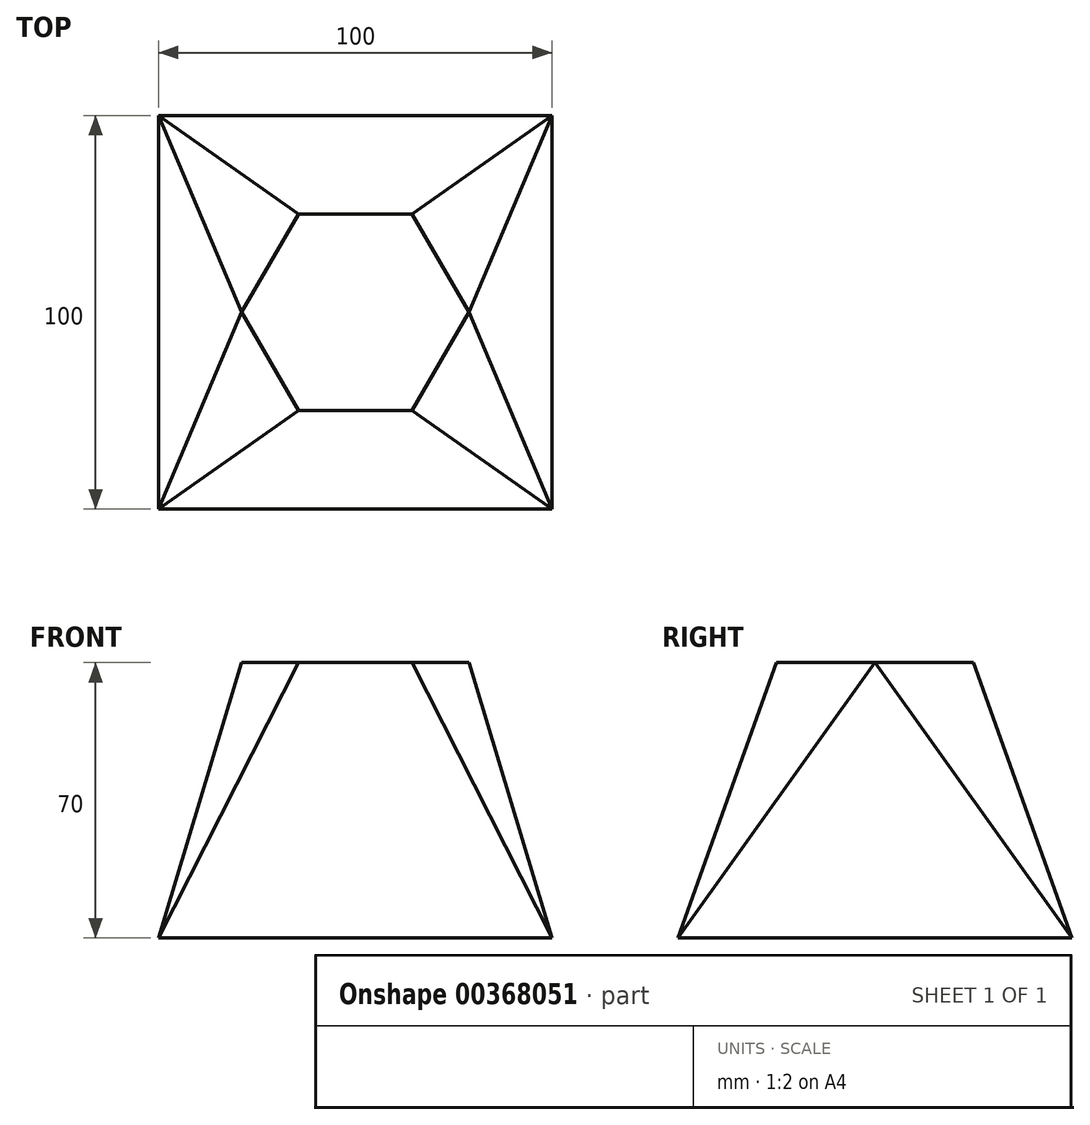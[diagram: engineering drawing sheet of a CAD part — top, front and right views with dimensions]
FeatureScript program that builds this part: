
annotation { "Feature Type Name" : "Feature", "Feature Type Description" : "" }
export const myFeature = defineFeature(function(context is Context, id is Id, definition is map)
    precondition{}
    {
        {
            var Q0;
            Q0=qCreatedBy(makeId("Top.planeOp"),FACE);
            var sketch = newSketch(context, id + "F0", { "sketchPlane" : qUnion([Q0])});
            skLineSegment(sketch, "E0.bottom", {"start": v(-50, 50) * mm, "end": v(50, 50) * mm});
            skLineSegment(sketch, "E0.top", {"start": v(-50, -50) * mm, "end": v(50, -50) * mm});
            skLineSegment(sketch, "E0.left", {"start": v(-50, 50) * mm, "end": v(-50, -50) * mm});
            skLineSegment(sketch, "E0.right", {"start": v(50, 50) * mm, "end": v(50, -50) * mm});
            skSolve(sketch);
        }
        {
            var Q0;
            Q0=qCreatedBy(makeId("Top.planeOp"),FACE);
            cPlane(context, id + "F1", {"entities" : qUnion([Q0]), "cplaneType" : CPlaneType.OFFSET, "offset" : 70 * mm, "width" : 150 * mm, "height" : 150 * mm});
        }
        {
            var Q0;
            Q0=qCreatedBy(id+"F1.planeOp",FACE);
            var sketch = newSketch(context, id + "F2", { "sketchPlane" : qUnion([Q0])});
            skCircle(sketch, "E1.cCircle", {"center": v(0, 0) * mm, "radius": 25 * mm, "construction": true});
            skLineSegment(sketch, "E1.0", {"start": v(-14.43, 25) * mm, "end": v(14.43, 25) * mm});
            skLineSegment(sketch, "E1.1", {"start": v(14.43, 25) * mm, "end": v(28.87, 0) * mm});
            skLineSegment(sketch, "E1.2", {"start": v(28.87, 0) * mm, "end": v(14.43, -25) * mm});
            skLineSegment(sketch, "E1.3", {"start": v(14.43, -25) * mm, "end": v(-14.43, -25) * mm});
            skLineSegment(sketch, "E1.4", {"start": v(-14.43, -25) * mm, "end": v(-28.87, 0) * mm});
            skLineSegment(sketch, "E1.5", {"start": v(-28.87, 0) * mm, "end": v(-14.43, 25) * mm});
            skPoint(sketch, "E1.0.midPoint", {"position": v(0, 25) * mm});
            skLineSegment(sketch, "E2", {"start": v(-14.43, 25) * mm, "end": v(-14.43, -25) * mm});
            skLineSegment(sketch, "E3", {"start": v(14.43, 25) * mm, "end": v(14.43, -25) * mm});
            skSolve(sketch);
        }
        {
            var Q0;
            Q0=makeQuery(id+"F0.imprint","IMPRINT",FACE,{"disambiguationData":[TD([[makeQuery(id+"F0.imprint","IMPRINT",EDGE,{"derivedFrom":sQuery(id+"F0.wireOp",EDGE,"E0.bottom")}),-1.0]])]});
            var Q1;
            Q1=makeQuery(id+"F2.imprint","IMPRINT",FACE,{"disambiguationData":[TD([[makeQuery(id+"F2.imprint","IMPRINT",EDGE,{"derivedFrom":sQuery(id+"F2.wireOp",EDGE,"E1.0")}),-1.0]])]});
            loft(context, id + "F3", {"sheetProfilesArray" : [{ "sheetProfileEntities" : qUnion([Q0]) }, { "sheetProfileEntities" : qUnion([Q1]) }]});
        }
        {
            var Q1;
            Q1=makeQuery(id+"F2.imprint","IMPRINT",FACE,{"disambiguationData":[TD([[makeQuery(id+"F2.imprint","IMPRINT",EDGE,{"derivedFrom":sQuery(id+"F2.wireOp",EDGE,"E1.4")}),-1.0]])]});
            var Q2;
            Q2=makeQuery(id+"F3.opLoft","MID_CAP_VERTEX",VERTEX,{"disambiguationData":[OSD([sQuery(id+"F0.wireOp",EDGE,"E0.bottom"),sQuery(id+"F0.wireOp",EDGE,"E0.left")])],"capPos":0.0});
            loft(context, id + "F4", {"operationType" : NewBodyOperationType.ADD, "sheetProfilesArray" : [{ "sheetProfileEntities" : qUnion([Q1]) }, { "sheetProfileEntities" : qUnion([Q2]) }]});
        }
        {
            var Q1;
            Q1=makeQuery(id+"F2.imprint","IMPRINT",FACE,{"disambiguationData":[TD([[makeQuery(id+"F2.imprint","IMPRINT",EDGE,{"derivedFrom":sQuery(id+"F2.wireOp",EDGE,"E1.4")}),-1.0]])]});
            var Q2;
            Q2=makeQuery(id+"F3.opLoft","MID_CAP_VERTEX",VERTEX,{"disambiguationData":[OSD([sQuery(id+"F0.wireOp",EDGE,"E0.top"),sQuery(id+"F0.wireOp",EDGE,"E0.left")])],"capPos":0.0});
            loft(context, id + "F5", {"operationType" : NewBodyOperationType.ADD, "sheetProfilesArray" : [{ "sheetProfileEntities" : qUnion([Q1]) }, { "sheetProfileEntities" : qUnion([Q2]) }]});
        }
        {
            var Q1;
            Q1=makeQuery(id+"F5.opLoft","SWEPT_FACE",FACE,{"disambiguationData":[OSD([sQuery(id+"F2.wireOp",EDGE,"E1.0"),sQuery(id+"F2.wireOp",EDGE,"E1.4"),sQuery(id+"F2.wireOp",EDGE,"E1.5"),sQuery(id+"F2.wireOp",EDGE,"E2")])]});
            var Q2;
            Q2=makeQuery(id+"F4.opLoft","SWEPT_FACE",FACE,{"disambiguationData":[OSD([sQuery(id+"F2.wireOp",EDGE,"E1.3"),sQuery(id+"F2.wireOp",EDGE,"E1.4"),sQuery(id+"F2.wireOp",EDGE,"E1.5"),sQuery(id+"F2.wireOp",EDGE,"E2")])]});
            var Q3;
            {var subQ0=sQuery(id+"F0.wireOp",EDGE,"E0.left");var subQ1=sQuery(id+"F0.wireOp",EDGE,"E0.top");Q3=makeQuery(id+"F5.boolean.opBoolean","MERGE",VERTEX,{"derivedFrom":[makeQuery(id+"F3.opLoft","MID_CAP_VERTEX",VERTEX,{"disambiguationData":[OSD([subQ1,subQ0])],"capPos":0.0}),makeQuery(id+"F5.opLoft","SWEPT_VERTEX",VERTEX,{"disambiguationData":[OSD([subQ1,subQ0,sQuery(id+"F2.wireOp",EDGE,"E1.3"),sQuery(id+"F2.wireOp",EDGE,"E1.4"),sQuery(id+"F2.wireOp",EDGE,"E2")])]})]});}
            var Q4;
            {var subQ0=sQuery(id+"F0.wireOp",EDGE,"E0.left");var subQ1=sQuery(id+"F0.wireOp",EDGE,"E0.bottom");Q4=makeQuery(id+"F4.boolean.opBoolean","MERGE",VERTEX,{"derivedFrom":[makeQuery(id+"F3.opLoft","MID_CAP_VERTEX",VERTEX,{"disambiguationData":[OSD([subQ1,subQ0])],"capPos":0.0}),makeQuery(id+"F4.opLoft","SWEPT_VERTEX",VERTEX,{"disambiguationData":[OSD([subQ1,subQ0,sQuery(id+"F2.wireOp",EDGE,"E1.3"),sQuery(id+"F2.wireOp",EDGE,"E1.4"),sQuery(id+"F2.wireOp",EDGE,"E2")])]})]});}
            loft(context, id + "F6", {"operationType" : NewBodyOperationType.ADD, "sheetProfilesArray" : [{ "sheetProfileEntities" : qUnion([Q1]) }, { "sheetProfileEntities" : qUnion([Q2]) }], "matchConnections" : true, "connections" : [{ "connectionEntities" : qUnion([Q3, Q4]), "connectionEdgeQueries" : qUnion([]), "connectionEdgeParameters" : [] }]});
        }
        {
            var Q1;
            Q1=makeQuery(id+"F2.imprint","IMPRINT",FACE,{"disambiguationData":[TD([[makeQuery(id+"F2.imprint","IMPRINT",EDGE,{"derivedFrom":sQuery(id+"F2.wireOp",EDGE,"E1.1")}),-1.0]])]});
            var Q2;
            Q2=makeQuery(id+"F3.opLoft","MID_CAP_VERTEX",VERTEX,{"disambiguationData":[OSD([sQuery(id+"F0.wireOp",EDGE,"E0.top"),sQuery(id+"F0.wireOp",EDGE,"E0.right")])],"capPos":0.0});
            loft(context, id + "F7", {"operationType" : NewBodyOperationType.ADD, "sheetProfilesArray" : [{ "sheetProfileEntities" : qUnion([Q1]) }, { "sheetProfileEntities" : qUnion([Q2]) }]});
        }
        {
            var Q1;
            Q1=makeQuery(id+"F2.imprint","IMPRINT",FACE,{"disambiguationData":[TD([[makeQuery(id+"F2.imprint","IMPRINT",EDGE,{"derivedFrom":sQuery(id+"F2.wireOp",EDGE,"E1.1")}),-1.0]])]});
            var Q2;
            Q2=makeQuery(id+"F3.opLoft","MID_CAP_VERTEX",VERTEX,{"disambiguationData":[OSD([sQuery(id+"F0.wireOp",EDGE,"E0.bottom"),sQuery(id+"F0.wireOp",EDGE,"E0.right")])],"capPos":0.0});
            loft(context, id + "F8", {"operationType" : NewBodyOperationType.ADD, "sheetProfilesArray" : [{ "sheetProfileEntities" : qUnion([Q1]) }, { "sheetProfileEntities" : qUnion([Q2]) }]});
        }
        {
            var Q1;
            Q1=makeQuery(id+"F8.opLoft","SWEPT_FACE",FACE,{"disambiguationData":[OSD([sQuery(id+"F2.wireOp",EDGE,"E1.1"),sQuery(id+"F2.wireOp",EDGE,"E1.2"),sQuery(id+"F2.wireOp",EDGE,"E1.3"),sQuery(id+"F2.wireOp",EDGE,"E3")])]});
            var Q2;
            Q2=makeQuery(id+"F7.opLoft","SWEPT_FACE",FACE,{"disambiguationData":[OSD([sQuery(id+"F2.wireOp",EDGE,"E1.0"),sQuery(id+"F2.wireOp",EDGE,"E1.1"),sQuery(id+"F2.wireOp",EDGE,"E1.2"),sQuery(id+"F2.wireOp",EDGE,"E3")])]});
            var Q3;
            {var subQ0=sQuery(id+"F0.wireOp",EDGE,"E0.right");var subQ1=sQuery(id+"F0.wireOp",EDGE,"E0.bottom");Q3=makeQuery(id+"F8.boolean.opBoolean","MERGE",VERTEX,{"derivedFrom":[makeQuery(id+"F3.opLoft","MID_CAP_VERTEX",VERTEX,{"disambiguationData":[OSD([subQ1,subQ0])],"capPos":0.0}),makeQuery(id+"F8.opLoft","SWEPT_VERTEX",VERTEX,{"disambiguationData":[OSD([subQ1,subQ0,sQuery(id+"F2.wireOp",EDGE,"E1.1"),sQuery(id+"F2.wireOp",EDGE,"E1.2")])]})]});}
            var Q4;
            {var subQ0=sQuery(id+"F0.wireOp",EDGE,"E0.right");var subQ1=sQuery(id+"F0.wireOp",EDGE,"E0.top");Q4=makeQuery(id+"F7.boolean.opBoolean","MERGE",VERTEX,{"derivedFrom":[makeQuery(id+"F3.opLoft","MID_CAP_VERTEX",VERTEX,{"disambiguationData":[OSD([subQ1,subQ0])],"capPos":0.0}),makeQuery(id+"F7.opLoft","SWEPT_VERTEX",VERTEX,{"disambiguationData":[OSD([subQ1,subQ0,sQuery(id+"F2.wireOp",EDGE,"E1.1"),sQuery(id+"F2.wireOp",EDGE,"E1.2")])]})]});}
            loft(context, id + "F9", {"operationType" : NewBodyOperationType.ADD, "sheetProfilesArray" : [{ "sheetProfileEntities" : qUnion([Q1]) }, { "sheetProfileEntities" : qUnion([Q2]) }], "matchConnections" : true, "connections" : [{ "connectionEntities" : qUnion([Q3, Q4]), "connectionEdgeQueries" : qUnion([]), "connectionEdgeParameters" : [] }]});
        }
    });
